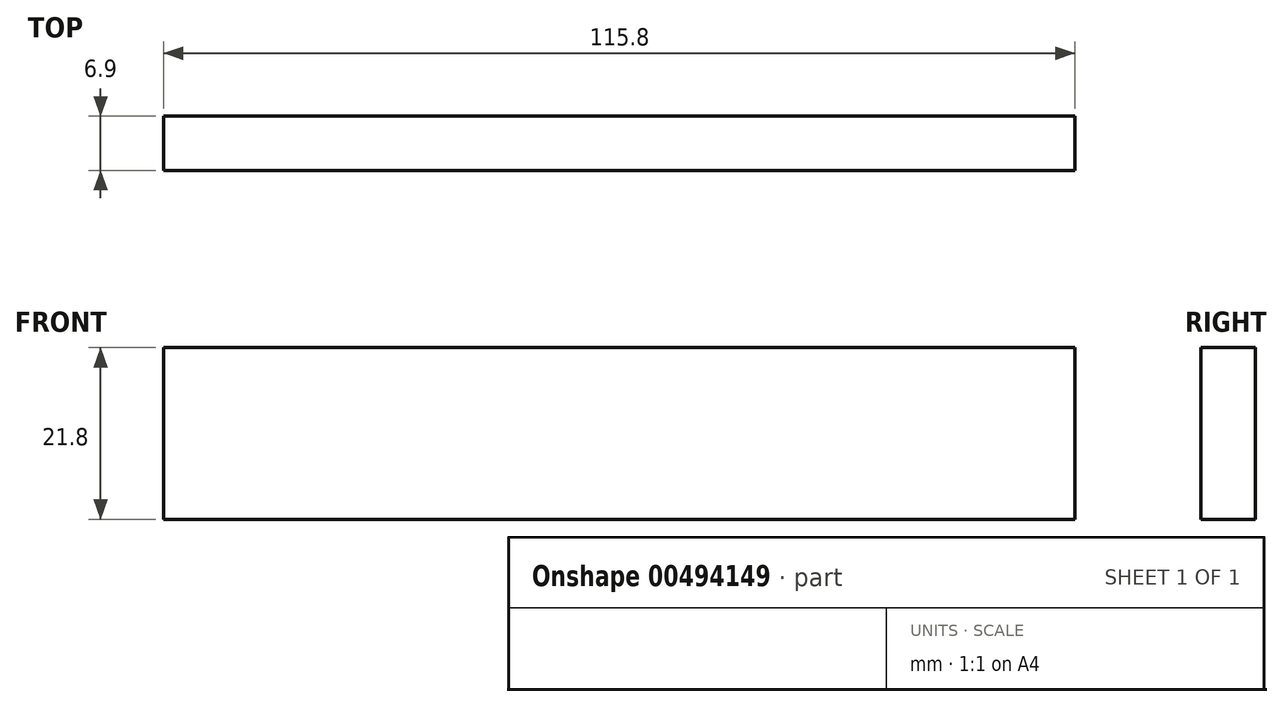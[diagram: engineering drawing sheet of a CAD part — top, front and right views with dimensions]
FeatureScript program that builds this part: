
annotation { "Feature Type Name" : "Feature", "Feature Type Description" : "" }
export const myFeature = defineFeature(function(context is Context, id is Id, definition is map)
    precondition{}
    {
        {
            var Q0;
            Q0=qCreatedBy(makeId("Front.planeOp"),FACE);
            var sketch = newSketch(context, id + "F0", { "sketchPlane" : qUnion([Q0])});
            skLineSegment(sketch, "E0.bottom", {"start": v(-55.65, 21.8) * mm, "end": v(60.15, 21.8) * mm});
            skLineSegment(sketch, "E0.top", {"start": v(-55.65, 0) * mm, "end": v(60.15, 0) * mm});
            skLineSegment(sketch, "E0.left", {"start": v(-55.65, 21.8) * mm, "end": v(-55.65, 0) * mm});
            skLineSegment(sketch, "E0.right", {"start": v(60.15, 21.8) * mm, "end": v(60.15, 0) * mm});
            skSolve(sketch);
        }
        {
            var Q0;
            Q0=makeQuery(id+"F0.imprint","IMPRINT",FACE,{"disambiguationData":[TD([[makeQuery(id+"F0.imprint","IMPRINT",EDGE,{"derivedFrom":sQuery(id+"F0.wireOp",EDGE,"E0.bottom")}),-1.0]])]});
            extrude(context, id + "F1", {"entities" : qUnion([Q0]), "depth" : 6.9 * mm});
        }
    });
